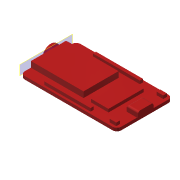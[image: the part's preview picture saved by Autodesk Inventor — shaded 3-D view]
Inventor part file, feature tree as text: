
AUTODESK INVENTOR PART (.ipt)
format: ipt  version: 2019 (Build 230136000, 136)  size: 217,088 bytes
history: native  units: mm
features: extrude x7, sketch x7, projected_geometry x5, fillet x1, plane x1
ambient origin geometry x8: Origin, YZ Plane, XZ Plane, XY Plane, X Axis, Y Axis, Z Axis, Center Point
bodies: Volumenkörper1 (feature_tree)
feature tree (21):
  extrude  "Extrusion1"  Depth=27.0mm
  extrude  "Extrusion2"  Depth=1.5mm TaperAngle=0.0deg
  fillet  "Rundung1"  Radius=5.5mm
  extrude  "Extrusion3"  Depth=0.5mm
  extrude  "Extrusion5"  Depth=1.0mm
  plane  "Arbeitsebene1"
  extrude  "Extrusion8"  Depth=17.0mm
  extrude  "Extrusion9"  Depth=15.0mm
  extrude  "Extrusion10"  Depth=13.0mm
  sketch  "Skizze1"  dims[d0=46.7mm d1=27.0mm]
  sketch  "Skizze2"  dims[d2=2.0mm d3=1.5mm d4=0.0mm d5=5.5mm]
  projected_geometry  "Projizierte Kontur1"
  sketch  "Skizze3"  dims[d6=7.5mm d7=0.5mm]
  projected_geometry  "Projizierte Kontur2"
  sketch  "Skizze5"  dims[d8=2.8mm d9=0.0mm d10=1.0mm]
  projected_geometry  "Projizierte Kontur4"
  sketch  "Skizze8"  dims[d11=25.5mm d12=17.0mm]
  sketch  "Skizze9"  dims[d13=2.8mm d14=0.0mm d23=15.0mm]
  projected_geometry  "Projizierte Kontur8"
  sketch  "Skizze10"  dims[d24=15.0mm d25=13.0mm d26=16.5mm d27=8.0mm d28=2.0mm d29=0.0mm d39=1.0mm d40=9.0mm d41=9.0mm d43=2.1mm d44=0.0mm d45=8.0mm d46=3.8mm d47=0.0mm d49=4.5mm d50=4.5mm d54=1.0mm d56=1.5mm d57=0.0mm d58=1.0mm d59=1.0mm d60=1.5mm d61=1.5mm d62=0.6mm]
  projected_geometry  "Projizierte Kontur10"
